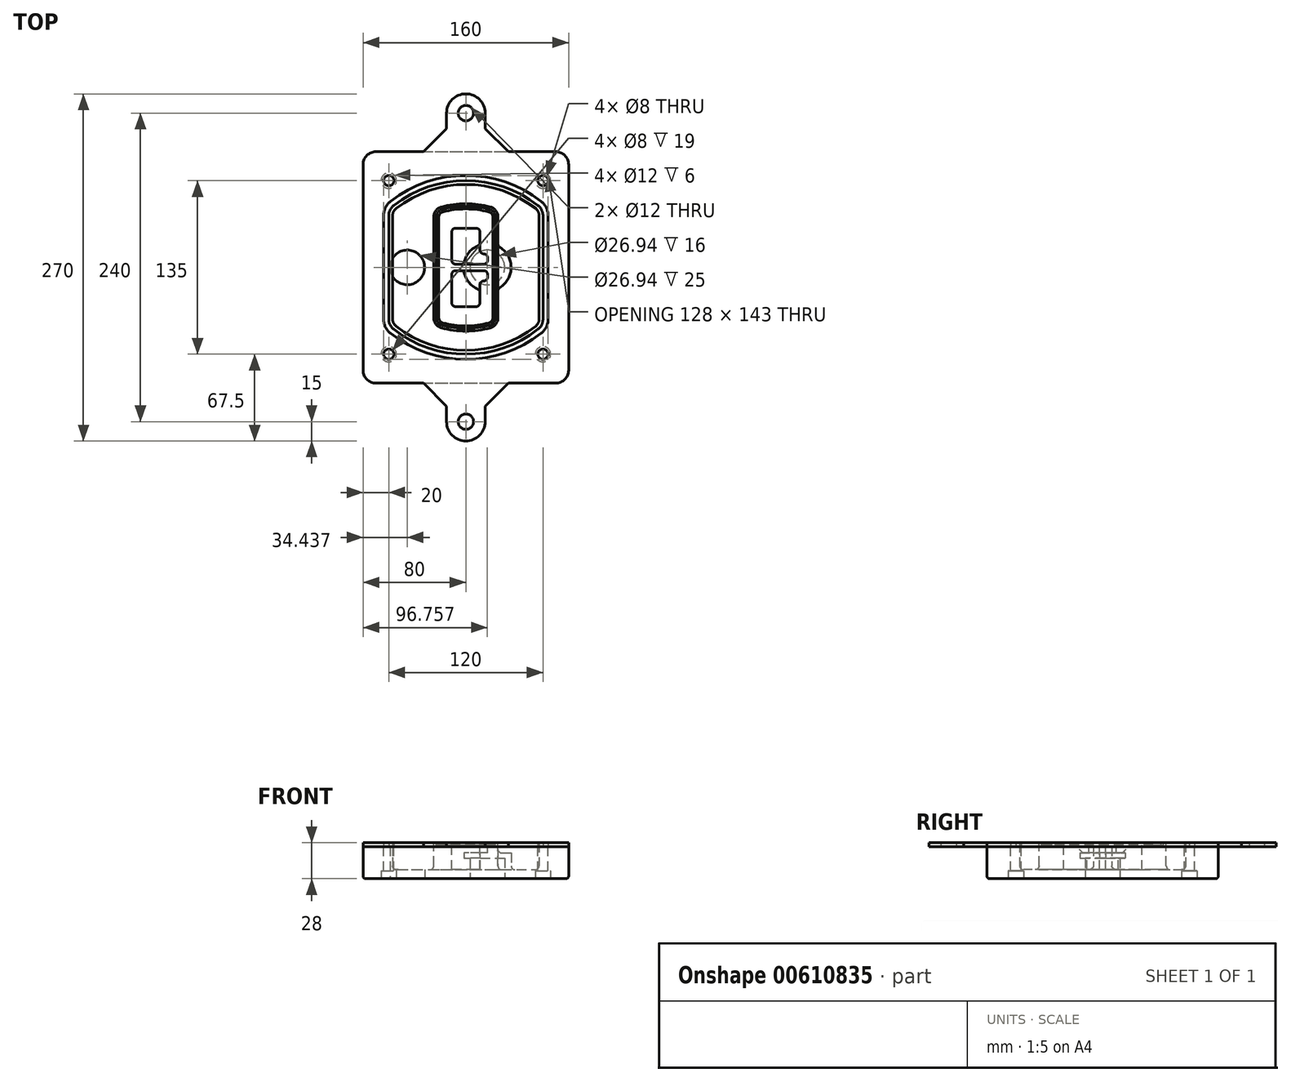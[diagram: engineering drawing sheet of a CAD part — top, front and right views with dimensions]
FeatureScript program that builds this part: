
annotation { "Feature Type Name" : "Feature", "Feature Type Description" : "" }
export const myFeature = defineFeature(function(context is Context, id is Id, definition is map)
    precondition{}
    {
        {
            var Q0;
            Q0=qCreatedBy(makeId("Top.planeOp"),FACE);
            var sketch = newSketch(context, id + "F0", { "sketchPlane" : qUnion([Q0])});
            skPoint(sketch, "E0.rect.middle", {"position": v(0, 0) * mm});
            skLineSegment(sketch, "E1.bottom", {"start": v(-70, -90) * mm, "end": v(70, -90) * mm});
            skLineSegment(sketch, "E1.top", {"start": v(-70, 90) * mm, "end": v(70, 90) * mm});
            skLineSegment(sketch, "E1.left", {"start": v(-80, -80) * mm, "end": v(-80, 80) * mm});
            skLineSegment(sketch, "E1.right", {"start": v(80, -80) * mm, "end": v(80, 80) * mm});
            skLineSegment(sketch, "E2", {"start": v(-80, 90) * mm, "end": v(80, -90) * mm, "construction": true});
            skLineSegment(sketch, "E3", {"start": v(80, 90) * mm, "end": v(-80, -90) * mm, "construction": true});
            skCircle(sketch, "E4", {"center": v(-60, 67.5) * mm, "radius": 4 * mm});
            skCircle(sketch, "E5", {"center": v(60, 67.5) * mm, "radius": 4 * mm});
            skCircle(sketch, "E6", {"center": v(60, -67.5) * mm, "radius": 4 * mm});
            skCircle(sketch, "E7", {"center": v(-60, -67.5) * mm, "radius": 4 * mm});
            skLineSegment(sketch, "E8", {"start": v(-60, 67.5) * mm, "end": v(60, 67.5) * mm, "construction": true});
            skLineSegment(sketch, "E9", {"start": v(60, 67.5) * mm, "end": v(60, -67.5) * mm, "construction": true});
            skLineSegment(sketch, "E10", {"start": v(60, -67.5) * mm, "end": v(-60, -67.5) * mm, "construction": true});
            skLineSegment(sketch, "E11", {"start": v(-60, -67.5) * mm, "end": v(-60, 67.5) * mm, "construction": true});
            skLineSegment(sketch, "E12", {"start": v(-60, 40.3) * mm, "end": v(-60, -40.3) * mm});
            skLineSegment(sketch, "E13", {"start": v(60, 40.3) * mm, "end": v(60, -40.3) * mm});
            skArc(sketch, "E14", {"start": v(56.15, 48.18) * mm, "mid": v(0, 67.5) * mm, "end": v(-56.15, 48.18) * mm});
            skArc(sketch, "E15", {"start": v(-56.15, -48.18) * mm, "mid": v(0, -67.5) * mm, "end": v(56.15, -48.18) * mm});
            skLineSegment(sketch, "E16", {"start": v(-60, 0) * mm, "end": v(60, 0) * mm, "construction": true});
            skPoint(sketch, "E17.visualSharp", {"position": v(-60, -45) * mm});
            skArc(sketch, "E17.filletArc", {"start": v(-60, -40.3) * mm, "mid": v(-58.99, -44.68) * mm, "end": v(-56.15, -48.18) * mm});
            skPoint(sketch, "E18.visualSharp", {"position": v(-60, 45) * mm});
            skArc(sketch, "E18.filletArc", {"start": v(-56.15, 48.18) * mm, "mid": v(-58.99, 44.68) * mm, "end": v(-60, 40.3) * mm});
            skPoint(sketch, "E19.visualSharp", {"position": v(60, 45) * mm});
            skArc(sketch, "E19.filletArc", {"start": v(60, 40.3) * mm, "mid": v(58.99, 44.68) * mm, "end": v(56.15, 48.18) * mm});
            skPoint(sketch, "E20.visualSharp", {"position": v(60, -45) * mm});
            skArc(sketch, "E20.filletArc", {"start": v(56.15, -48.18) * mm, "mid": v(58.99, -44.68) * mm, "end": v(60, -40.3) * mm});
            skPoint(sketch, "E21.visualSharp", {"position": v(-80, 90) * mm});
            skArc(sketch, "E21.filletArc", {"start": v(-70, 90) * mm, "mid": v(-77.07, 87.07) * mm, "end": v(-80, 80) * mm});
            skPoint(sketch, "E22.visualSharp", {"position": v(80, 90) * mm});
            skArc(sketch, "E22.filletArc", {"start": v(80, 80) * mm, "mid": v(77.07, 87.07) * mm, "end": v(70, 90) * mm});
            skPoint(sketch, "E23.visualSharp", {"position": v(80, -90) * mm});
            skArc(sketch, "E23.filletArc", {"start": v(70, -90) * mm, "mid": v(77.07, -87.07) * mm, "end": v(80, -80) * mm});
            skPoint(sketch, "E24.visualSharp", {"position": v(-80, -90) * mm});
            skArc(sketch, "E24.filletArc", {"start": v(-80, -80) * mm, "mid": v(-77.07, -87.07) * mm, "end": v(-70, -90) * mm});
            skArc(sketch, "E25.0", {"start": v(57, 40.3) * mm, "mid": v(56.3, 43.36) * mm, "end": v(54.3, 45.81) * mm});
            skLineSegment(sketch, "E25.1", {"start": v(57, 40.3) * mm, "end": v(57, -40.3) * mm});
            skArc(sketch, "E25.2", {"start": v(54.3, -45.81) * mm, "mid": v(56.3, -43.36) * mm, "end": v(57, -40.3) * mm});
            skArc(sketch, "E25.3", {"start": v(-54.3, -45.81) * mm, "mid": v(0, -64.5) * mm, "end": v(54.3, -45.81) * mm});
            skArc(sketch, "E25.4", {"start": v(-57, -40.3) * mm, "mid": v(-56.3, -43.36) * mm, "end": v(-54.3, -45.81) * mm});
            skArc(sketch, "E25.5", {"start": v(54.3, 45.81) * mm, "mid": v(0, 64.5) * mm, "end": v(-54.3, 45.81) * mm});
            skLineSegment(sketch, "E25.6", {"start": v(-57, 40.3) * mm, "end": v(-57, -40.3) * mm});
            skArc(sketch, "E25.7", {"start": v(-54.3, 45.81) * mm, "mid": v(-56.3, 43.36) * mm, "end": v(-57, 40.3) * mm});
            skArc(sketch, "E26.0", {"start": v(-58.62, 51.33) * mm, "mid": v(-62.58, 46.43) * mm, "end": v(-64, 40.3) * mm});
            skArc(sketch, "E26.1", {"start": v(58.62, 51.33) * mm, "mid": v(0, 71.5) * mm, "end": v(-58.62, 51.33) * mm});
            skArc(sketch, "E26.2", {"start": v(64, 40.3) * mm, "mid": v(62.58, 46.43) * mm, "end": v(58.62, 51.33) * mm});
            skLineSegment(sketch, "E26.3", {"start": v(64, 40.3) * mm, "end": v(64, -40.3) * mm});
            skArc(sketch, "E26.4", {"start": v(58.62, -51.33) * mm, "mid": v(62.58, -46.43) * mm, "end": v(64, -40.3) * mm});
            skLineSegment(sketch, "E26.5", {"start": v(-64, 40.3) * mm, "end": v(-64, -40.3) * mm});
            skArc(sketch, "E26.6", {"start": v(-58.62, -51.33) * mm, "mid": v(0, -71.5) * mm, "end": v(58.62, -51.33) * mm});
            skArc(sketch, "E26.7", {"start": v(-64, -40.3) * mm, "mid": v(-62.58, -46.43) * mm, "end": v(-58.62, -51.33) * mm});
            skLineSegment(sketch, "E27", {"start": v(0, 90) * mm, "end": v(0, 120) * mm, "construction": true});
            skPoint(sketch, "E27.endSnap0", {"position": v(0, 90) * mm});
            skCircle(sketch, "E28", {"center": v(0, 120) * mm, "radius": 6 * mm});
            skLineSegment(sketch, "E29", {"start": v(-33, 90) * mm, "end": v(-15, 108) * mm});
            skLineSegment(sketch, "E30", {"start": v(33, 90) * mm, "end": v(15, 108) * mm});
            skLineSegment(sketch, "E31", {"start": v(-15, 108) * mm, "end": v(-15, 120) * mm});
            skLineSegment(sketch, "E32", {"start": v(15, 108) * mm, "end": v(15, 120) * mm});
            skArc(sketch, "E33", {"start": v(15, 120) * mm, "mid": v(0, 135) * mm, "end": v(-15, 120) * mm});
            skLineSegment(sketch, "E34.MirrorCS", {"start": v(33, -90) * mm, "end": v(15, -108) * mm});
            skLineSegment(sketch, "E35.MirrorCS", {"start": v(15, -108) * mm, "end": v(15, -120) * mm});
            skArc(sketch, "E36.MirrorCS", {"start": v(15, -120) * mm, "mid": v(0, -135) * mm, "end": v(-15, -120) * mm});
            skLineSegment(sketch, "E37.MirrorCS", {"start": v(-15, -108) * mm, "end": v(-15, -120) * mm});
            skLineSegment(sketch, "E38.MirrorCS", {"start": v(-33, -90) * mm, "end": v(-15, -108) * mm});
            skCircle(sketch, "E39.MirrorC", {"center": v(0, -120) * mm, "radius": 6 * mm});
            skSolve(sketch);
        }
        {
            var Q0;
            Q0=makeQuery(id+"F0.imprint","IMPRINT",FACE,{"disambiguationData":[TD([[makeQuery(id+"F0.imprint","IMPRINT",EDGE,{"derivedFrom":sQuery(id+"F0.wireOp",EDGE,"E1.bottom")}),1.0]])]});
            var Q1;
            Q1=makeQuery(id+"F0.imprint","IMPRINT",FACE,{"disambiguationData":[TD([[makeQuery(id+"F0.imprint","IMPRINT",EDGE,{"derivedFrom":sQuery(id+"F0.wireOp",EDGE,"E12")}),1.0]])]});
            var Q2;
            Q2=makeQuery(id+"F0.imprint","IMPRINT",FACE,{"disambiguationData":[TD([[makeQuery(id+"F0.imprint","IMPRINT",EDGE,{"derivedFrom":sQuery(id+"F0.wireOp",EDGE,"E25.0")}),1.0]])]});
            var Q3;
            Q3=makeQuery(id+"F0.imprint","IMPRINT",FACE,{"disambiguationData":[TD([[makeQuery(id+"F0.imprint","IMPRINT",EDGE,{"derivedFrom":sQuery(id+"F0.wireOp",EDGE,"E12")}),-1.0]])]});
            extrude(context, id + "F1", {"entities" : qUnion([Q0, Q1, Q2, Q3]), "oppositeDirection" : true, "depth" : 25 * mm});
        }
        {
            var Q0;
            Q0=makeQuery(id+"F0.imprint","IMPRINT",FACE,{"disambiguationData":[TD([[makeQuery(id+"F0.imprint","IMPRINT",EDGE,{"derivedFrom":sQuery(id+"F0.wireOp",EDGE,"E12")}),1.0]])]});
            extrude(context, id + "F2", {"entities" : qUnion([Q0]), "operationType" : NewBodyOperationType.ADD, "depth" : 3 * mm});
        }
        {
            var Q0;
            Q0=makeQuery(id+"F0.imprint","IMPRINT",FACE,{"disambiguationData":[TD([[makeQuery(id+"F0.imprint","IMPRINT",EDGE,{"derivedFrom":sQuery(id+"F0.wireOp",EDGE,"E25.0")}),1.0]])]});
            extrude(context, id + "F3", {"entities" : qUnion([Q0]), "operationType" : NewBodyOperationType.REMOVE, "oppositeDirection" : true, "depth" : 18 * mm});
        }
        {
            var Q0;
            Q0=makeQuery(id+"F2.opExtrude","CAP_FACE",FACE,{"disambiguationData":[OSD([sQuery(id+"F0.wireOp",EDGE,"E12"),sQuery(id+"F0.wireOp",EDGE,"E13"),sQuery(id+"F0.wireOp",EDGE,"E14"),sQuery(id+"F0.wireOp",EDGE,"E15"),sQuery(id+"F0.wireOp",EDGE,"E17.filletArc"),sQuery(id+"F0.wireOp",EDGE,"E18.filletArc"),sQuery(id+"F0.wireOp",EDGE,"E19.filletArc"),sQuery(id+"F0.wireOp",EDGE,"E20.filletArc"),sQuery(id+"F0.wireOp",EDGE,"E25.0"),sQuery(id+"F0.wireOp",EDGE,"E25.1"),sQuery(id+"F0.wireOp",EDGE,"E25.2"),sQuery(id+"F0.wireOp",EDGE,"E25.3"),sQuery(id+"F0.wireOp",EDGE,"E25.4"),sQuery(id+"F0.wireOp",EDGE,"E25.5"),sQuery(id+"F0.wireOp",EDGE,"E25.6"),sQuery(id+"F0.wireOp",EDGE,"E25.7")])],"isStart":false});
            var sketch = newSketch(context, id + "F4", { "sketchPlane" : qUnion([Q0])});
            skArc(sketch, "E40.0", {"start": v(-19.08, -46.97) * mm, "mid": v(0, -49.5) * mm, "end": v(19.08, -46.97) * mm});
            skArc(sketch, "E41.0", {"start": v(19.08, 46.97) * mm, "mid": v(0, 49.5) * mm, "end": v(-19.08, 46.97) * mm});
            skLineSegment(sketch, "E42", {"start": v(-25, 39.25) * mm, "end": v(-25, -39.25) * mm});
            skLineSegment(sketch, "E43", {"start": v(25, 39.25) * mm, "end": v(25, -39.25) * mm});
            skLineSegment(sketch, "E44", {"start": v(-25, 45.1) * mm, "end": v(25, 45.1) * mm, "construction": true});
            skLineSegment(sketch, "E45", {"start": v(-25, -45.1) * mm, "end": v(25, -45.1) * mm, "construction": true});
            skPoint(sketch, "E46.visualSharp", {"position": v(-25, 45.1) * mm});
            skArc(sketch, "E46.filletArc", {"start": v(-19.08, 46.97) * mm, "mid": v(-23.35, 44.11) * mm, "end": v(-25, 39.25) * mm});
            skPoint(sketch, "E47.visualSharp", {"position": v(25, 45.1) * mm});
            skArc(sketch, "E47.filletArc", {"start": v(25, 39.25) * mm, "mid": v(23.35, 44.11) * mm, "end": v(19.08, 46.97) * mm});
            skPoint(sketch, "E48.visualSharp", {"position": v(25, -45.1) * mm});
            skArc(sketch, "E48.filletArc", {"start": v(19.08, -46.97) * mm, "mid": v(23.35, -44.11) * mm, "end": v(25, -39.25) * mm});
            skPoint(sketch, "E49.visualSharp", {"position": v(-25, -45.1) * mm});
            skArc(sketch, "E49.filletArc", {"start": v(-25, -39.25) * mm, "mid": v(-23.35, -44.11) * mm, "end": v(-19.08, -46.97) * mm});
            skArc(sketch, "E50.0", {"start": v(54.3, 45.81) * mm, "mid": v(0, 64.5) * mm, "end": v(-54.3, 45.81) * mm});
            skArc(sketch, "E50.1", {"start": v(-54.3, 45.81) * mm, "mid": v(-56.3, 43.36) * mm, "end": v(-57, 40.3) * mm});
            skLineSegment(sketch, "E50.2", {"start": v(-57, 40.3) * mm, "end": v(-57, -40.3) * mm});
            skArc(sketch, "E50.3", {"start": v(-57, -40.3) * mm, "mid": v(-56.3, -43.36) * mm, "end": v(-54.3, -45.81) * mm});
            skArc(sketch, "E50.4", {"start": v(-54.3, -45.81) * mm, "mid": v(0, -64.5) * mm, "end": v(54.3, -45.81) * mm});
            skArc(sketch, "E50.5", {"start": v(54.3, -45.81) * mm, "mid": v(56.3, -43.36) * mm, "end": v(57, -40.3) * mm});
            skLineSegment(sketch, "E50.6", {"start": v(57, 40.3) * mm, "end": v(57, -40.3) * mm});
            skArc(sketch, "E50.7", {"start": v(57, 40.3) * mm, "mid": v(56.3, 43.36) * mm, "end": v(54.3, 45.81) * mm});
            skLineSegment(sketch, "E51.0", {"start": v(23, 39.25) * mm, "end": v(23, -39.25) * mm});
            skArc(sketch, "E51.1", {"start": v(18.56, -45.04) * mm, "mid": v(21.76, -42.9) * mm, "end": v(23, -39.25) * mm});
            skArc(sketch, "E51.2", {"start": v(-18.56, -45.04) * mm, "mid": v(0, -47.5) * mm, "end": v(18.56, -45.04) * mm});
            skArc(sketch, "E51.3", {"start": v(-23, -39.25) * mm, "mid": v(-21.76, -42.9) * mm, "end": v(-18.56, -45.04) * mm});
            skLineSegment(sketch, "E51.4", {"start": v(-23, 39.25) * mm, "end": v(-23, -39.25) * mm});
            skArc(sketch, "E51.5", {"start": v(23, 39.25) * mm, "mid": v(21.76, 42.9) * mm, "end": v(18.56, 45.04) * mm});
            skArc(sketch, "E51.6", {"start": v(-18.56, 45.04) * mm, "mid": v(-21.76, 42.9) * mm, "end": v(-23, 39.25) * mm});
            skArc(sketch, "E51.7", {"start": v(18.56, 45.04) * mm, "mid": v(0, 47.5) * mm, "end": v(-18.56, 45.04) * mm});
            skArc(sketch, "E52.0", {"start": v(21, 39.25) * mm, "mid": v(20.18, 41.68) * mm, "end": v(18.04, 43.1) * mm});
            skLineSegment(sketch, "E52.1", {"start": v(21, 39.25) * mm, "end": v(21, -39.25) * mm});
            skArc(sketch, "E52.2", {"start": v(18.04, -43.1) * mm, "mid": v(20.18, -41.68) * mm, "end": v(21, -39.25) * mm});
            skArc(sketch, "E52.3", {"start": v(-18.04, -43.1) * mm, "mid": v(0, -45.5) * mm, "end": v(18.04, -43.1) * mm});
            skArc(sketch, "E52.4", {"start": v(-21, -39.25) * mm, "mid": v(-20.18, -41.68) * mm, "end": v(-18.04, -43.1) * mm});
            skArc(sketch, "E52.5", {"start": v(18.04, 43.1) * mm, "mid": v(0, 45.5) * mm, "end": v(-18.04, 43.1) * mm});
            skLineSegment(sketch, "E52.6", {"start": v(-21, 39.25) * mm, "end": v(-21, -39.25) * mm});
            skArc(sketch, "E52.7", {"start": v(-18.04, 43.1) * mm, "mid": v(-20.18, 41.68) * mm, "end": v(-21, 39.25) * mm});
            skLineSegment(sketch, "E53", {"start": v(-25, 0) * mm, "end": v(25, 0) * mm, "construction": true});
            skLineSegment(sketch, "E54", {"start": v(-11, 5.5) * mm, "end": v(-11, 27.5) * mm});
            skLineSegment(sketch, "E55", {"start": v(-8, 30.5) * mm, "end": v(8, 30.5) * mm});
            skLineSegment(sketch, "E56", {"start": v(11, 27.5) * mm, "end": v(11, 13.5) * mm});
            skLineSegment(sketch, "E57", {"start": v(14, 10.5) * mm, "end": v(14, 10.5) * mm});
            skLineSegment(sketch, "E58", {"start": v(17, 7.5) * mm, "end": v(17, 5.5) * mm});
            skLineSegment(sketch, "E59", {"start": v(14, 2.5) * mm, "end": v(-8, 2.5) * mm});
            skPoint(sketch, "E60.visualSharp", {"position": v(-11, 30.5) * mm});
            skArc(sketch, "E60.filletArc", {"start": v(-8, 30.5) * mm, "mid": v(-10.12, 29.62) * mm, "end": v(-11, 27.5) * mm});
            skPoint(sketch, "E61.visualSharp", {"position": v(11, 30.5) * mm});
            skArc(sketch, "E61.filletArc", {"start": v(11, 27.5) * mm, "mid": v(10.12, 29.62) * mm, "end": v(8, 30.5) * mm});
            skPoint(sketch, "E62.visualSharp", {"position": v(11, 10.5) * mm});
            skArc(sketch, "E62.filletArc", {"start": v(11, 13.5) * mm, "mid": v(11.88, 11.38) * mm, "end": v(14, 10.5) * mm});
            skPoint(sketch, "E63.visualSharp", {"position": v(17, 10.5) * mm});
            skArc(sketch, "E63.filletArc", {"start": v(17, 7.5) * mm, "mid": v(16.12, 9.62) * mm, "end": v(14, 10.5) * mm});
            skPoint(sketch, "E64.visualSharp", {"position": v(17, 2.5) * mm});
            skArc(sketch, "E64.filletArc", {"start": v(14, 2.5) * mm, "mid": v(16.12, 3.38) * mm, "end": v(17, 5.5) * mm});
            skPoint(sketch, "E65.visualSharp", {"position": v(-11, 2.5) * mm});
            skArc(sketch, "E65.filletArc", {"start": v(-11, 5.5) * mm, "mid": v(-10.12, 3.38) * mm, "end": v(-8, 2.5) * mm});
            skLineSegment(sketch, "E66.0.MirrorCS", {"start": v(14, -2.5) * mm, "end": v(-8, -2.5) * mm});
            skArc(sketch, "E67.0.MirrorCS", {"start": v(-11, -5.5) * mm, "mid": v(-10.12, -3.38) * mm, "end": v(-8, -2.5) * mm});
            skLineSegment(sketch, "E68.0.MirrorCS", {"start": v(-11, -5.5) * mm, "end": v(-11, -27.5) * mm});
            skArc(sketch, "E69.0.MirrorCS", {"start": v(-8, -30.5) * mm, "mid": v(-10.12, -29.62) * mm, "end": v(-11, -27.5) * mm});
            skLineSegment(sketch, "E70.0.MirrorCS", {"start": v(-8, -30.5) * mm, "end": v(8, -30.5) * mm});
            skArc(sketch, "E71.0.MirrorCS", {"start": v(11, -27.5) * mm, "mid": v(10.12, -29.62) * mm, "end": v(8, -30.5) * mm});
            skLineSegment(sketch, "E72.0.MirrorCS", {"start": v(11, -27.5) * mm, "end": v(11, -13.5) * mm});
            skArc(sketch, "E73.0.MirrorCS", {"start": v(11, -13.5) * mm, "mid": v(11.88, -11.38) * mm, "end": v(14, -10.5) * mm});
            skArc(sketch, "E74.0.MirrorCS", {"start": v(17, -7.5) * mm, "mid": v(16.12, -9.62) * mm, "end": v(14, -10.5) * mm});
            skLineSegment(sketch, "E75.0.MirrorCS", {"start": v(17, -7.5) * mm, "end": v(17, -5.5) * mm});
            skArc(sketch, "E76.0.MirrorCS", {"start": v(14, -2.5) * mm, "mid": v(16.12, -3.38) * mm, "end": v(17, -5.5) * mm});
            skSolve(sketch);
        }
        {
            var Q0;
            Q0=makeQuery(id+"F4.imprint","IMPRINT",FACE,{"disambiguationData":[TD([[makeQuery(id+"F4.imprint","IMPRINT",EDGE,{"derivedFrom":sQuery(id+"F4.wireOp",EDGE,"E40.0")}),1.0]])]});
            var Q1;
            Q1=makeQuery(id+"F4.imprint","IMPRINT",FACE,{"disambiguationData":[TD([[makeQuery(id+"F4.imprint","IMPRINT",EDGE,{"derivedFrom":sQuery(id+"F4.wireOp",EDGE,"E51.0")}),-1.0]])]});
            var Q2;
            Q2=makeQuery(id+"F4.imprint","IMPRINT",FACE,{"disambiguationData":[TD([[makeQuery(id+"F4.imprint","IMPRINT",EDGE,{"derivedFrom":sQuery(id+"F4.wireOp",EDGE,"E52.0")}),1.0]])]});
            extrude(context, id + "F5", {"entities" : qUnion([Q0, Q1, Q2]), "operationType" : NewBodyOperationType.ADD, "endBound" : BoundingType.UP_TO_NEXT, "oppositeDirection" : true, "depth" : 25 * mm});
        }
        {
            var Q0;
            Q0=makeQuery(id+"F4.imprint","IMPRINT",FACE,{"disambiguationData":[TD([[makeQuery(id+"F4.imprint","IMPRINT",EDGE,{"derivedFrom":sQuery(id+"F4.wireOp",EDGE,"E51.0")}),-1.0]])]});
            extrude(context, id + "F6", {"entities" : qUnion([Q0]), "operationType" : NewBodyOperationType.REMOVE, "oppositeDirection" : true, "depth" : 2 * mm});
        }
        {
            var Q0;
            Q0=makeQuery(id+"F1.opExtrude","CAP_FACE",FACE,{"disambiguationData":[OSD([sQuery(id+"F0.wireOp",EDGE,"E1.bottom"),sQuery(id+"F0.wireOp",EDGE,"E1.top"),sQuery(id+"F0.wireOp",EDGE,"E1.left"),sQuery(id+"F0.wireOp",EDGE,"E1.right"),sQuery(id+"F0.wireOp",EDGE,"E4"),sQuery(id+"F0.wireOp",EDGE,"E5"),sQuery(id+"F0.wireOp",EDGE,"E6"),sQuery(id+"F0.wireOp",EDGE,"E7"),sQuery(id+"F0.wireOp",EDGE,"E21.filletArc"),sQuery(id+"F0.wireOp",EDGE,"E22.filletArc"),sQuery(id+"F0.wireOp",EDGE,"E23.filletArc"),sQuery(id+"F0.wireOp",EDGE,"E24.filletArc")])],"isStart":false});
            var sketch = newSketch(context, id + "F7", { "sketchPlane" : qUnion([Q0])});
            skCircle(sketch, "E77", {"center": v(16.76, 0) * mm, "radius": 13.47 * mm});
            skCircle(sketch, "E78", {"center": v(-45.56, 0) * mm, "radius": 13.47 * mm});
            skLineSegment(sketch, "E79", {"start": v(80, 0) * mm, "end": v(-80, 0) * mm});
            skCircle(sketch, "E80", {"center": v(16.76, 0) * mm, "radius": 18.47 * mm});
            skCircle(sketch, "E81", {"center": v(60, -67.5) * mm, "radius": 6 * mm});
            skCircle(sketch, "E82", {"center": v(-60, -67.5) * mm, "radius": 6 * mm});
            skCircle(sketch, "E83", {"center": v(-60, 67.5) * mm, "radius": 6 * mm});
            skCircle(sketch, "E84", {"center": v(60, 67.5) * mm, "radius": 6 * mm});
            skSolve(sketch);
        }
        {
            var Q0;
            {var subQ1=sQuery(id+"F7.wireOp",EDGE,"E79");var subQ4=sQuery(id+"F7.wireOp",EDGE,"E77");var subQ6=makeQuery(id+"F7.imprint","INTERSECT",VERTEX,{"disambiguationData":[OD(0.0)],"derivedFrom":[subQ4,subQ1]});Q0=makeQuery(id+"F7.imprint","IMPRINT",FACE,{"disambiguationData":[TD([[makeQuery(id+"F7.imprint","IMPRINT",EDGE,{"disambiguationData":[TD([[subQ6,-1.0]])],"derivedFrom":subQ4}),-1.0]])]});}
            var Q1;
            {var subQ0=sQuery(id+"F7.wireOp",EDGE,"E79");var subQ1=sQuery(id+"F7.wireOp",EDGE,"E77");var subQ3=makeQuery(id+"F7.imprint","INTERSECT",VERTEX,{"disambiguationData":[OD(0.0)],"derivedFrom":[subQ1,subQ0]});Q1=makeQuery(id+"F7.imprint","IMPRINT",FACE,{"disambiguationData":[TD([[makeQuery(id+"F7.imprint","IMPRINT",EDGE,{"disambiguationData":[TD([[subQ3,-1.0]])],"derivedFrom":subQ1}),1.0]])]});}
            var Q2;
            {var subQ0=sQuery(id+"F7.wireOp",EDGE,"E79");var subQ1=sQuery(id+"F7.wireOp",EDGE,"E77");var subQ3=makeQuery(id+"F7.imprint","INTERSECT",VERTEX,{"disambiguationData":[OD(0.0)],"derivedFrom":[subQ1,subQ0]});Q2=makeQuery(id+"F7.imprint","IMPRINT",FACE,{"disambiguationData":[TD([[makeQuery(id+"F7.imprint","IMPRINT",EDGE,{"disambiguationData":[TD([[subQ3,1.0]])],"derivedFrom":subQ1}),1.0]])]});}
            var Q3;
            {var subQ1=sQuery(id+"F7.wireOp",EDGE,"E79");var subQ4=sQuery(id+"F7.wireOp",EDGE,"E77");var subQ6=makeQuery(id+"F7.imprint","INTERSECT",VERTEX,{"disambiguationData":[OD(0.0)],"derivedFrom":[subQ4,subQ1]});Q3=makeQuery(id+"F7.imprint","IMPRINT",FACE,{"disambiguationData":[TD([[makeQuery(id+"F7.imprint","IMPRINT",EDGE,{"disambiguationData":[TD([[subQ6,1.0]])],"derivedFrom":subQ4}),-1.0]])]});}
            extrude(context, id + "F8", {"entities" : qUnion([Q0, Q1, Q2, Q3]), "operationType" : NewBodyOperationType.ADD, "oppositeDirection" : true, "depth" : 20 * mm});
        }
        {
            var Q0;
            {var subQ0=sQuery(id+"F7.wireOp",EDGE,"E79");var subQ1=sQuery(id+"F7.wireOp",EDGE,"E77");var subQ3=makeQuery(id+"F7.imprint","INTERSECT",VERTEX,{"disambiguationData":[OD(0.0)],"derivedFrom":[subQ1,subQ0]});Q0=makeQuery(id+"F7.imprint","IMPRINT",FACE,{"disambiguationData":[TD([[makeQuery(id+"F7.imprint","IMPRINT",EDGE,{"disambiguationData":[TD([[subQ3,-1.0]])],"derivedFrom":subQ1}),1.0]])]});}
            var Q1;
            {var subQ0=sQuery(id+"F7.wireOp",EDGE,"E79");var subQ1=sQuery(id+"F7.wireOp",EDGE,"E77");var subQ3=makeQuery(id+"F7.imprint","INTERSECT",VERTEX,{"disambiguationData":[OD(0.0)],"derivedFrom":[subQ1,subQ0]});Q1=makeQuery(id+"F7.imprint","IMPRINT",FACE,{"disambiguationData":[TD([[makeQuery(id+"F7.imprint","IMPRINT",EDGE,{"disambiguationData":[TD([[subQ3,1.0]])],"derivedFrom":subQ1}),1.0]])]});}
            extrude(context, id + "F9", {"entities" : qUnion([Q0, Q1]), "operationType" : NewBodyOperationType.REMOVE, "oppositeDirection" : true, "depth" : 16 * mm});
        }
        {
            var Q0;
            {var subQ0=sQuery(id+"F7.wireOp",EDGE,"E79");var subQ1=sQuery(id+"F7.wireOp",EDGE,"E78");var subQ3=makeQuery(id+"F7.imprint","INTERSECT",VERTEX,{"disambiguationData":[OD(0.0)],"derivedFrom":[subQ1,subQ0]});Q0=makeQuery(id+"F7.imprint","IMPRINT",FACE,{"disambiguationData":[TD([[makeQuery(id+"F7.imprint","IMPRINT",EDGE,{"disambiguationData":[TD([[subQ3,-1.0]])],"derivedFrom":subQ1}),1.0]])]});}
            var Q1;
            {var subQ0=sQuery(id+"F7.wireOp",EDGE,"E79");var subQ1=sQuery(id+"F7.wireOp",EDGE,"E78");var subQ3=makeQuery(id+"F7.imprint","INTERSECT",VERTEX,{"disambiguationData":[OD(0.0)],"derivedFrom":[subQ1,subQ0]});Q1=makeQuery(id+"F7.imprint","IMPRINT",FACE,{"disambiguationData":[TD([[makeQuery(id+"F7.imprint","IMPRINT",EDGE,{"disambiguationData":[TD([[subQ3,1.0]])],"derivedFrom":subQ1}),1.0]])]});}
            extrude(context, id + "F10", {"entities" : qUnion([Q0, Q1]), "operationType" : NewBodyOperationType.REMOVE, "oppositeDirection" : true, "depth" : 25 * mm});
        }
        {
            var Q0;
            Q0=makeQuery(id+"F7.imprint","IMPRINT",FACE,{"disambiguationData":[TD([[makeQuery(id+"F7.imprint","IMPRINT",EDGE,{"derivedFrom":sQuery(id+"F7.wireOp",EDGE,"E81")}),1.0]])]});
            var Q1;
            Q1=makeQuery(id+"F7.imprint","IMPRINT",FACE,{"disambiguationData":[TD([[makeQuery(id+"F7.imprint","IMPRINT",EDGE,{"derivedFrom":makeQuery(id+"F1.opExtrude","CAP_EDGE",EDGE,{"disambiguationData":[OSD([sQuery(id+"F0.wireOp",EDGE,"E5")])],"isStart":false})}),-1.0]])]});
            var Q2;
            Q2=makeQuery(id+"F7.imprint","IMPRINT",FACE,{"disambiguationData":[TD([[makeQuery(id+"F7.imprint","IMPRINT",EDGE,{"derivedFrom":sQuery(id+"F7.wireOp",EDGE,"E82")}),1.0]])]});
            var Q3;
            Q3=makeQuery(id+"F7.imprint","IMPRINT",FACE,{"disambiguationData":[TD([[makeQuery(id+"F7.imprint","IMPRINT",EDGE,{"derivedFrom":makeQuery(id+"F1.opExtrude","CAP_EDGE",EDGE,{"disambiguationData":[OSD([sQuery(id+"F0.wireOp",EDGE,"E4")])],"isStart":false})}),-1.0]])]});
            var Q4;
            Q4=makeQuery(id+"F7.imprint","IMPRINT",FACE,{"disambiguationData":[TD([[makeQuery(id+"F7.imprint","IMPRINT",EDGE,{"derivedFrom":sQuery(id+"F7.wireOp",EDGE,"E83")}),1.0]])]});
            var Q5;
            Q5=makeQuery(id+"F7.imprint","IMPRINT",FACE,{"disambiguationData":[TD([[makeQuery(id+"F7.imprint","IMPRINT",EDGE,{"derivedFrom":makeQuery(id+"F1.opExtrude","CAP_EDGE",EDGE,{"disambiguationData":[OSD([sQuery(id+"F0.wireOp",EDGE,"E7")])],"isStart":false})}),-1.0]])]});
            var Q6;
            Q6=makeQuery(id+"F7.imprint","IMPRINT",FACE,{"disambiguationData":[TD([[makeQuery(id+"F7.imprint","IMPRINT",EDGE,{"derivedFrom":sQuery(id+"F7.wireOp",EDGE,"E84")}),1.0]])]});
            var Q7;
            Q7=makeQuery(id+"F7.imprint","IMPRINT",FACE,{"disambiguationData":[TD([[makeQuery(id+"F7.imprint","IMPRINT",EDGE,{"derivedFrom":makeQuery(id+"F1.opExtrude","CAP_EDGE",EDGE,{"disambiguationData":[OSD([sQuery(id+"F0.wireOp",EDGE,"E6")])],"isStart":false})}),-1.0]])]});
            extrude(context, id + "F11", {"entities" : qUnion([Q0, Q1, Q2, Q3, Q4, Q5, Q6, Q7]), "operationType" : NewBodyOperationType.REMOVE, "oppositeDirection" : true, "depth" : 6 * mm});
        }
        {
            var Q0;
            Q0=makeQuery(id+"F9.boolean.opBoolean","COPY",FACE,{"derivedFrom":makeQuery(id+"F9.opExtrude","CAP_FACE",FACE,{"disambiguationData":[OSD([sQuery(id+"F7.wireOp",EDGE,"E77")])],"isStart":false})});
            var sketch = newSketch(context, id + "F12", { "sketchPlane" : qUnion([Q0])});
            skArc(sketch, "E85.0", {"start": v(11, 17.55) * mm, "mid": v(2.57, 11.82) * mm, "end": v(-1.54, 2.5) * mm});
            skArc(sketch, "E85.1", {"start": v(-1.54, -2.5) * mm, "mid": v(2.57, -11.82) * mm, "end": v(11, -17.55) * mm});
            skLineSegment(sketch, "E86", {"start": v(-1.54, -2.5) * mm, "end": v(14, -2.5) * mm});
            skLineSegment(sketch, "E87.0", {"start": v(14, 2.5) * mm, "end": v(-1.54, 2.5) * mm});
            skArc(sketch, "E87.1", {"start": v(14, 2.5) * mm, "mid": v(16.12, 3.38) * mm, "end": v(17, 5.5) * mm});
            skLineSegment(sketch, "E87.2", {"start": v(17, 7.5) * mm, "end": v(17, 5.5) * mm});
            skArc(sketch, "E87.3", {"start": v(17, 7.5) * mm, "mid": v(16.12, 9.62) * mm, "end": v(14, 10.5) * mm});
            skArc(sketch, "E87.4", {"start": v(11, 13.5) * mm, "mid": v(11.88, 11.38) * mm, "end": v(14, 10.5) * mm});
            skLineSegment(sketch, "E87.5", {"start": v(11, 17.55) * mm, "end": v(11, 13.5) * mm});
            skLineSegment(sketch, "E87.7", {"start": v(14, -2.5) * mm, "end": v(-1.54, -2.5) * mm});
            skArc(sketch, "E87.8", {"start": v(14, -2.5) * mm, "mid": v(16.12, -3.38) * mm, "end": v(17, -5.5) * mm});
            skLineSegment(sketch, "E87.9", {"start": v(17, -7.5) * mm, "end": v(17, -5.5) * mm});
            skArc(sketch, "E87.10", {"start": v(17, -7.5) * mm, "mid": v(16.12, -9.62) * mm, "end": v(14, -10.5) * mm});
            skArc(sketch, "E87.11", {"start": v(11, -13.5) * mm, "mid": v(11.88, -11.38) * mm, "end": v(14, -10.5) * mm});
            skLineSegment(sketch, "E87.12", {"start": v(11, -17.55) * mm, "end": v(11, -13.5) * mm});
            skPoint(sketch, "E88.orphan", {"position": v(11, -27.5) * mm});
            skPoint(sketch, "E89.orphan", {"position": v(-8, -2.5) * mm});
            skPoint(sketch, "E90.orphan", {"position": v(-8, 2.5) * mm});
            skPoint(sketch, "E91.orphan", {"position": v(11, 27.5) * mm});
            skSolve(sketch);
        }
        {
            var Q0;
            {var subQ7=sQuery(id+"F12.wireOp",EDGE,"E85.0");var subQ14=sQuery(id+"F12.wireOp",EDGE,"E85.1");var subQ16=sQuery(id+"F12.wireOp",EDGE,"E87.1");var subQ18=sQuery(id+"F12.wireOp",EDGE,"E87.8");Q0=qUnion([makeQuery(id+"F12.imprint","IMPRINT",FACE,{"disambiguationData":[TD([[makeQuery(id+"F12.imprint","IMPRINT",EDGE,{"derivedFrom":subQ7}),1.0]])]}),makeQuery(id+"F12.imprint","IMPRINT",FACE,{"disambiguationData":[TD([[makeQuery(id+"F12.imprint","IMPRINT",EDGE,{"derivedFrom":subQ14}),1.0]])]}),makeQuery(id+"F12.imprint","IMPRINT",FACE,{"disambiguationData":[TD([[makeQuery(id+"F12.imprint","IMPRINT",EDGE,{"derivedFrom":subQ16}),1.0]])]}),makeQuery(id+"F12.imprint","IMPRINT",FACE,{"disambiguationData":[TD([[makeQuery(id+"F12.imprint","IMPRINT",EDGE,{"derivedFrom":subQ18}),-1.0]])]})]);}
            var Q1;
            Q1=makeQuery(id+"F5.boolean.opBoolean","SPLIT",FACE,{"disambiguationData":[TD([makeQuery(id+"F5.opExtrude","SWEPT_FACE",FACE,{"disambiguationData":[OSD([sQuery(id+"F4.wireOp",EDGE,"E54")])]})])],"derivedFrom":makeQuery(id+"F3.boolean.opBoolean","COPY",FACE,{"derivedFrom":makeQuery(id+"F3.opExtrude","CAP_FACE",FACE,{"disambiguationData":[OSD([sQuery(id+"F0.wireOp",EDGE,"E25.0"),sQuery(id+"F0.wireOp",EDGE,"E25.1"),sQuery(id+"F0.wireOp",EDGE,"E25.2"),sQuery(id+"F0.wireOp",EDGE,"E25.3"),sQuery(id+"F0.wireOp",EDGE,"E25.4"),sQuery(id+"F0.wireOp",EDGE,"E25.5"),sQuery(id+"F0.wireOp",EDGE,"E25.6"),sQuery(id+"F0.wireOp",EDGE,"E25.7")])],"isStart":false})})});
            extrude(context, id + "F13", {"entities" : qUnion([Q0]), "operationType" : NewBodyOperationType.REMOVE, "endBound" : BoundingType.UP_TO_SURFACE, "endBoundEntityFace" : qUnion([Q1]), "depth" : 25 * mm});
        }
        {
            var Q0;
            Q0=makeQuery(id+"F3.boolean.opBoolean","COPY",EDGE,{"derivedFrom":makeQuery(id+"F3.opExtrude","CAP_EDGE",EDGE,{"disambiguationData":[OSD([sQuery(id+"F0.wireOp",EDGE,"E25.6")])],"isStart":false})});
            var Q1;
            Q1=makeQuery(id+"F8.boolean.opBoolean","INTERSECT",EDGE,{"derivedFrom":[makeQuery(id+"F5.opExtrude","SWEPT_FACE",FACE,{"disambiguationData":[OSD([sQuery(id+"F4.wireOp",EDGE,"E43")])]}),makeQuery(id+"F8.opExtrude","CAP_FACE",FACE,{"disambiguationData":[OSD([sQuery(id+"F7.wireOp",EDGE,"E80")])],"isStart":false})]});
            var Q2;
            Q2=makeQuery(id+"F8.boolean.opBoolean","INTERSECT",EDGE,{"disambiguationData":[OD(1.0)],"derivedFrom":[makeQuery(id+"F5.opExtrude","SWEPT_FACE",FACE,{"disambiguationData":[OSD([sQuery(id+"F4.wireOp",EDGE,"E43")])]}),makeQuery(id+"F8.opExtrude","SWEPT_FACE",FACE,{"disambiguationData":[OSD([sQuery(id+"F7.wireOp",EDGE,"E80")])]})]});
            var Q3;
            {var subQ0=sQuery(id+"F4.wireOp",EDGE,"E43");Q3=makeQuery(id+"F8.boolean.opBoolean","SPLIT",EDGE,{"disambiguationData":[TD([makeQuery(id+"F5.opExtrude","SWEPT_FACE",FACE,{"disambiguationData":[OSD([sQuery(id+"F4.wireOp",EDGE,"E48.filletArc")])]})])],"derivedFrom":makeQuery(id+"F5.opExtrude","CAP_EDGE",EDGE,{"disambiguationData":[OSD([subQ0])],"isStart":false})});}
            var Q4;
            {var subQ0=sQuery(id+"F0.wireOp",EDGE,"E25.7");var subQ1=sQuery(id+"F0.wireOp",EDGE,"E25.1");var subQ2=sQuery(id+"F0.wireOp",EDGE,"E25.6");var subQ3=sQuery(id+"F0.wireOp",EDGE,"E25.5");var subQ4=sQuery(id+"F0.wireOp",EDGE,"E25.4");var subQ5=sQuery(id+"F0.wireOp",EDGE,"E25.0");var subQ6=sQuery(id+"F0.wireOp",EDGE,"E25.2");var subQ7=sQuery(id+"F0.wireOp",EDGE,"E25.3");Q4=makeQuery(id+"F8.boolean.opBoolean","INTERSECT",EDGE,{"derivedFrom":[makeQuery(id+"F5.boolean.opBoolean","SPLIT",FACE,{"disambiguationData":[TD([makeQuery(id+"F2.opExtrude","SWEPT_FACE",FACE,{"disambiguationData":[OSD([subQ5])]})])],"derivedFrom":makeQuery(id+"F3.boolean.opBoolean","COPY",FACE,{"derivedFrom":makeQuery(id+"F3.opExtrude","CAP_FACE",FACE,{"disambiguationData":[OSD([subQ5,subQ1,subQ6,subQ7,subQ4,subQ3,subQ2,subQ0])],"isStart":false})})}),makeQuery(id+"F8.opExtrude","SWEPT_FACE",FACE,{"disambiguationData":[OSD([sQuery(id+"F7.wireOp",EDGE,"E80")])]})]});}
            var Q5;
            Q5=makeQuery(id+"F8.boolean.opBoolean","INTERSECT",EDGE,{"disambiguationData":[OD(0.0)],"derivedFrom":[makeQuery(id+"F5.opExtrude","SWEPT_FACE",FACE,{"disambiguationData":[OSD([sQuery(id+"F4.wireOp",EDGE,"E43")])]}),makeQuery(id+"F8.opExtrude","SWEPT_FACE",FACE,{"disambiguationData":[OSD([sQuery(id+"F7.wireOp",EDGE,"E80")])]})]});
            fillet(context, id + "F14", {"entities" : qUnion([Q0, Q1, Q2, Q3, Q4, Q5]), "radius" : 3 * mm, "tangentPropagation" : true, "allowEdgeOverflow" : false});
        }
        {
            var Q0;
            Q0=makeQuery(id+"F1.opExtrude","CAP_EDGE",EDGE,{"disambiguationData":[OSD([sQuery(id+"F0.wireOp",EDGE,"E1.bottom")])],"isStart":false});
            fillet(context, id + "F15", {"entities" : qUnion([Q0]), "radius" : 2 * mm, "tangentPropagation" : true, "allowEdgeOverflow" : false});
        }
        {
            var Q0;
            Q0 = qSketchRegion(id + "F0", true);
            var Q1;
            Q1=makeQuery(id+"F2.opExtrude","CAP_FACE",FACE,{"disambiguationData":[OSD([sQuery(id+"F0.wireOp",EDGE,"E12"),sQuery(id+"F0.wireOp",EDGE,"E13"),sQuery(id+"F0.wireOp",EDGE,"E14"),sQuery(id+"F0.wireOp",EDGE,"E15"),sQuery(id+"F0.wireOp",EDGE,"E17.filletArc"),sQuery(id+"F0.wireOp",EDGE,"E18.filletArc"),sQuery(id+"F0.wireOp",EDGE,"E19.filletArc"),sQuery(id+"F0.wireOp",EDGE,"E20.filletArc"),sQuery(id+"F0.wireOp",EDGE,"E25.0"),sQuery(id+"F0.wireOp",EDGE,"E25.1"),sQuery(id+"F0.wireOp",EDGE,"E25.2"),sQuery(id+"F0.wireOp",EDGE,"E25.3"),sQuery(id+"F0.wireOp",EDGE,"E25.4"),sQuery(id+"F0.wireOp",EDGE,"E25.5"),sQuery(id+"F0.wireOp",EDGE,"E25.6"),sQuery(id+"F0.wireOp",EDGE,"E25.7")])],"isStart":false});
            extrude(context, id + "F16", {"entities" : qUnion([Q0]), "endBound" : BoundingType.UP_TO_SURFACE, "depth" : 25 * mm, "endBoundEntityFace" : qUnion([Q1]), "offsetDistance" : 25 * mm});
        }
    });
